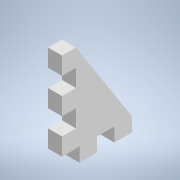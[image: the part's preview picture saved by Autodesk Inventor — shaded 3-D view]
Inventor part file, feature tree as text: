
AUTODESK INVENTOR PART (.ipt)
format: ipt  version: 2020.2 (Build 242310000, 310)  size: 134,656 bytes
history: native  units: mm
features: extrude x2, sketch x2
ambient origin geometry x8: Origin, YZ Plane, XZ Plane, XY Plane, X Axis, Y Axis, Z Axis, Center Point
bodies: Solido1 (feature_tree)
feature tree (4):
  extrude  "Estrusione1"  Depth=16.0mm
  extrude  "Estrusione2"  Depth=25.0mm
  sketch  "Schizzo1"
  sketch  "Schizzo2"
